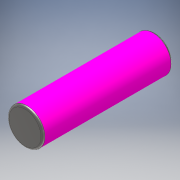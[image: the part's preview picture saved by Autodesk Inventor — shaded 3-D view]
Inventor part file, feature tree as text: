
AUTODESK INVENTOR PART (.ipt)
format: ipt  version: 2018.3 (Build 223285000, 285)  size: 115,200 bytes
history: native  units: mm
features: other x1, extrude x1, fillet x1, sketch x1
ambient origin geometry x8: Origin, YZ Plane, XZ Plane, XY Plane, X Axis, Y Axis, Z Axis, Center Point
bodies: Body1 (feature_tree)
feature tree (4):
  other  "Sólido1"
  extrude  "Extrusión1"  Depth=65.0mm TaperAngle=0.0deg
  fillet  "Empalme1"  Radius=1.0mm
  sketch  "Boceto1"  dims[d0=18.0mm d1=65.0mm d2=0.0mm d3=1.0mm]
